# Revit family: Faucet-Kitchen_Sink-KOHLER-Artifacts-K-99261
name_source: partatom
category: Plumbing Fixtures
revit_build: Autodesk Revit 2015 (Build: 20140606_1530(x64)
units: mm (PartAtom-declared; Revit-internal decimal feet)

## types (4) — shared parameters
ADA Compliant = Yes
Assembly Code = D2020
Cold Water Inlet = Cold Water Inlet
Date Modified = 02/27/2018
Default Elevation = 36"
Description = Single-hole kitchen sink faucet with 16 inch pull-down spout and turned lever handle, DockNetik magnetic docking system, and 3-function sprayhead featuring Sweep and BerrySoft spray
Faucet Hole Spacing = 0"
Flow Rate = 2 GPM
Height = 15 29/32"
Hot Water Inlet = Hot Water Inlet
Length = 10 1/32"
Manufacturer = KOHLER Co.
MasterFormat 1995 = 15410
MasterFormat 2004 = 22.41.39
Material = Premium Metal Construction
Pressure = 60.00 psi
Product Documentation Link = http://www.us.kohler.com
Product Name = Artifacts
Product Page URL = http://www.us.kohler.com
Spout Reach = 7 9/16"
URL = https://www.us.kohler.com
Vent Connection = No
Waste Connection = No
Waste Water Outlet = Waste Water Outlet
Width = 5 1/8"

## per-type parameters (varying)
| type | CW Connection | Finish | HW Connection | Model | Type |
| CP- Polished Chrome | Yes | Kohler-Metal-CP-Polished_Chrome | Yes | K-99261-CP | 1 |
| SN- Vibrant Polished Nickel | No | Kohler-Metal-SN-Vibrant_Polished_Nickel | No | K-99261-SN | 2 |
| VS- Vibrant Stainless | No | Kohler-Metal-VS-Vibrant_Stainless | No | K-99261-VS | 3 |
| 2BZ- Oil- Rubbed Bronze | No | Kohler-Metal-2BZ-Oil_Rubbed_Bronze | No | K-99261-2BZ | 4 |

## geometry (parser evidence)
native form markers: Sweep x53
no freeform markers — native parametric forms only
